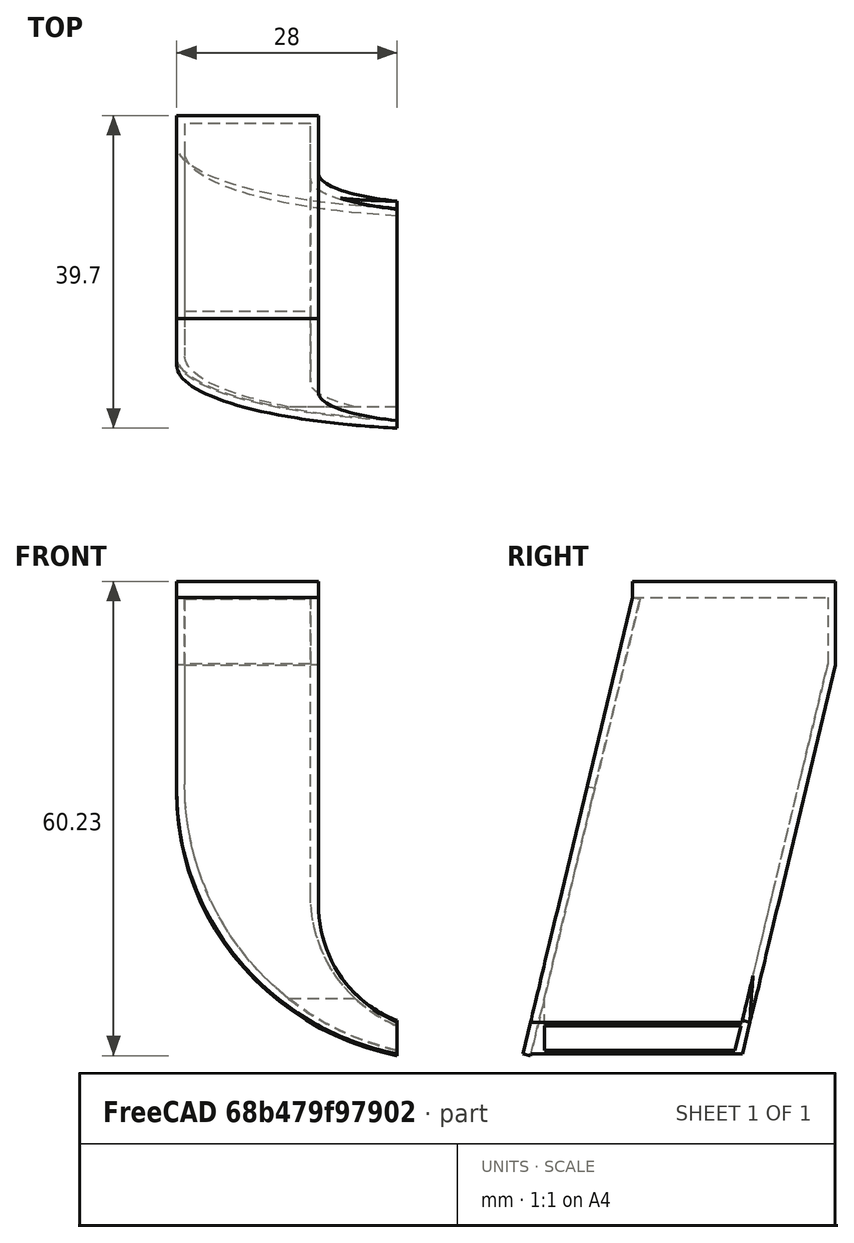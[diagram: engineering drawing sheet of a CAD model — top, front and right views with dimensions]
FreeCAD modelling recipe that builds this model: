
FCSTD DOCUMENT  (FreeCAD 0.19R)
Label: FanDuct9.2
License: All rights reserved
LicenseURL: http://en.wikipedia.org/wiki/All_rights_reserved
objects: Sketcher::SketchObject×15, PartDesign::Pad×5, PartDesign::Pocket×4, PartDesign::Body×1
note: 34 computed .brp shape members not serialized (recipe doc carries the construction recipe); baked Part::Feature solids carry a one-line shape summary decoded from their .brp

FEATURE [Sketcher::SketchObject] Sketch
  FullyConstrained = true
  MapMode = 5
  Support = -> [XY_Plane]
  sketch-geometry (5):
    g0: LineSegment StartX=0 StartY=0 StartZ=0 EndX=44 EndY=0 EndZ=0
    g1: LineSegment StartX=-14 StartY=0 StartZ=0 EndX=0 EndY=0 EndZ=0
    g2: LineSegment StartX=-14 StartY=0 StartZ=0 EndX=-14 EndY=-60.5 EndZ=0
    g3: LineSegment StartX=-14 StartY=-60.5 StartZ=0 EndX=44 EndY=-60.5 EndZ=0
    g4: LineSegment StartX=44 StartY=-60.5 StartZ=0 EndX=44 EndY=0 EndZ=0
  constraints (14):
    c: Coincident(g-1,g0)
    c: PointOnObject(g0,g-1)
    c: PointOnObject(g1,g-1)
    c: Coincident(g1,g0)
    c: Coincident(g1,g2)
    c: Vertical(g2)
    c: Coincident(g2,g3)
    c: Horizontal(g3)
    c: Coincident(g3,g4)
    c: Coincident(g4,g0)
    c: Vertical(g4)
    c: Distance(g4) = 60.5
    c: DistanceX(g0) = 44
    c: DistanceX(g1) = -14
FEATURE [Sketcher::SketchObject] Sketch035  label="startingpos"
  FullyConstrained = true
  MapMode = 5
  Placement = pos=(-14,0,0) rot=(0.57735,-0.57735,-0.57735;2.0944rad)
  sketch-geometry (9):
    g0: Circle CenterX=35 CenterY=-20 CenterZ=0 NormalX=0 NormalY=0 NormalZ=1 AngleXU=0 Radius=1
    g1: Circle CenterX=12 CenterY=44 CenterZ=0 NormalX=0 NormalY=0 NormalZ=1 AngleXU=0 Radius=1.9
    g2: Circle CenterX=55 CenterY=44 CenterZ=0 NormalX=0 NormalY=0 NormalZ=1 AngleXU=0 Radius=1.9
    g3: LineSegment StartX=12.5 StartY=38 StartZ=0 EndX=35 EndY=38 EndZ=0
    g4: LineSegment StartX=11 StartY=39 StartZ=0 EndX=59 EndY=39 EndZ=0
    g5: LineSegment StartX=59 StartY=39 StartZ=0 EndX=59 EndY=-19 EndZ=0
    g6: LineSegment StartX=59 StartY=-19 StartZ=0 EndX=11 EndY=-19 EndZ=0
    g7: LineSegment StartX=11 StartY=-19 StartZ=0 EndX=11 EndY=39 EndZ=0
    g8: GeomPoint X=35 Y=-19 Z=0
  constraints (26):
    c: DistanceY(g0) = -20
    c: Diameter(g1) = 3.8
    c: Equal(g1,g2)
    c: DistanceX(g1) = 12
    c: DistanceY(g1) = 44
    c: DistanceX(g2) = 55
    c: DistanceY(g2) = 44
    c: Diameter(g0) = 2
    c: Horizontal(g3)
    c: Distance(g3) = 22.5
    c: DistanceX(g0) = 35
    c: DistanceX(g3) = 35
    c: DistanceY(g3) = 38
    c: Coincident(g4,g5)
    c: Coincident(g5,g6)
    c: Coincident(g6,g7)
    c: Coincident(g7,g4)
    c: Horizontal(g4)
    c: Horizontal(g6)
    c: Vertical(g5)
    c: Vertical(g7)
    c: Distance(g6) = 48
    c: Symmetric(g6,g5,g8)
    c: DistanceX(g8) = 35
    c: DistanceY(g4) = 39
    c: DistanceY(g6) = -19
FEATURE [PartDesign::Pad] Pad
  Direction = (1,1,1)
  Length = 18
  Length2 = 10
  Placement = pos=(-14,0,0) rot=(0.57735,-0.57735,-0.57735;2.0944rad)
  Profile = -> Sketch035
  Type = 4
FEATURE [Sketcher::SketchObject] Sketch037  label="startingpos001"
  ExternalGeometry = -> [Pad]
  FullyConstrained = false
  MapMode = 5
  Placement = pos=(-32,0,2e-15) rot=(0.57735,-0.57735,-0.57735;2.0944rad)
  Support = -> [Pad]
  sketch-geometry (11):
    g0: Circle CenterX=35 CenterY=-20 CenterZ=0 NormalX=0 NormalY=0 NormalZ=1 AngleXU=0 Radius=1
    g1: Circle CenterX=12 CenterY=44 CenterZ=0 NormalX=0 NormalY=0 NormalZ=1 AngleXU=0 Radius=1.9
    g2: Circle CenterX=55 CenterY=44 CenterZ=0 NormalX=0 NormalY=0 NormalZ=1 AngleXU=0 Radius=1.9
    g3: LineSegment StartX=12.5 StartY=38 StartZ=0 EndX=35 EndY=38 EndZ=0
    g4: LineSegment StartX=5.2832 StartY=54.2913 StartZ=0 EndX=25.5067 EndY=-30.1947 EndZ=0
    g5: LineSegment StartX=25.5067 StartY=-30.1947 StartZ=0 EndX=-54.6701 EndY=-30.1947 EndZ=0
    g6: LineSegment StartX=-54.6701 StartY=-30.1947 StartZ=0 EndX=-35.1899 EndY=60.5708 EndZ=0
    g7: LineSegment StartX=-35.1899 StartY=60.5708 StartZ=0 EndX=99.6909 EndY=60.5708 EndZ=0
    g8: LineSegment StartX=63.1501 StartY=-71.009 StartZ=0 EndX=31.7121 EndY=60.3269 EndZ=0
    g9: LineSegment StartX=31.7121 StartY=60.3269 StartZ=0 EndX=5.2832 EndY=54.2913 EndZ=0
    g10: LineSegment StartX=63.1501 StartY=-71.009 StartZ=0 EndX=99.6909 EndY=60.5708 EndZ=0
  constraints (32):
    c: DistanceY(g0) = -20
    c: Diameter(g1) = 3.8
    c: Equal(g1,g2)
    c: DistanceX(g1) = 12
    c: DistanceY(g1) = 44
    c: DistanceX(g2) = 55
    c: DistanceY(g2) = 44
    c: Diameter(g0) = 2
    c: Horizontal(g3)
    c: Distance(g3) = 22.5
    c: DistanceX(g0) = 35
    c: DistanceX(g3) = 35
    c: DistanceY(g3) = 38
    c: Horizontal(g5)
    c: Coincident(g5,g6)
    c: Coincident(g6,g7)
    c: Horizontal(g7)
    c: Coincident(g8,g9)
    c: Coincident(g9,g4)
    c: Distance(g3,g8) = 2
    c: Coincident(g5,g4)
    c: Coincident(g8,g10)
    c: Coincident(g10,g7)
    c: DistanceX(g8) = 63.1501
    c: DistanceX(g4) = 25.5067
    c: DistanceX(g7) = 99.6909
    c: DistanceY(g7) = 60.5708
    c: DistanceX(g6) = -35.1899
    c: DistanceX(g5) = -54.6701
    c: DistanceX(g8) = 31.7121
    c: Distance(g-4,g4) = 2
    c: Parallel(g8,g4)
FEATURE [PartDesign::Pocket] Pocket
  BaseFeature = -> Pad
  Length = 5
  Length2 = 100
  Placement = pos=(-14,0,0) rot=(0.57735,-0.57735,-0.57735;2.0944rad)
  Profile = -> Sketch037
  Type = 1
FEATURE [Sketcher::SketchObject] Sketch038
  FullyConstrained = true
  MapMode = 5
  Placement = pos=(-14,-11,1.2e-15) rot=(0.57735,-0.57735,-0.57735;4.18879rad)
  Support = -> [Pocket]
  sketch-geometry (4):
    g0: LineSegment StartX=-54.22 StartY=0 StartZ=0 EndX=7.1e-15 EndY=0 EndZ=0
    g1: LineSegment StartX=-54.22 StartY=0 StartZ=0 EndX=-54.22 EndY=-31.06 EndZ=0
    g2: LineSegment StartX=-54.22 StartY=-31.06 StartZ=0 EndX=6.64 EndY=-31.06 EndZ=0
    g3: ArcOfCircle CenterX=2e-15 CenterY=-16.2397 CenterZ=0 NormalX=0 NormalY=0 NormalZ=1 AngleXU=0 Radius=16.2397 StartAngle=5.13361 EndAngle=7.85398
  constraints (11):
    c: Coincident(g0,g1)
    c: Vertical(g1)
    c: Coincident(g1,g2)
    c: Horizontal(g2)
    c: Coincident(g0,g-1)
    c: Tangent(g3,g0) = 1.5708
    c: PointOnObject(g0,g-1)
    c: Coincident(g2,g3)
    c: DistanceX(g1) = -54.22
    c: Distance(g1) = 31.06
    c: DistanceX(g2) = 6.64
FEATURE [PartDesign::Pocket] Pocket001
  BaseFeature = -> Pocket
  Length = 5
  Length2 = 100
  Placement = pos=(-14,0,0) rot=(0.57735,-0.57735,-0.57735;2.0944rad)
  Profile = -> Sketch038
  Type = 1
FEATURE [Sketcher::SketchObject] Sketch039
  ExternalGeometry = -> [Pocket001]
  FullyConstrained = true
  MapMode = 5
  Placement = pos=(-14,-11,1.2e-15) rot=(0.57735,-0.57735,-0.57735;4.18879rad)
  Support = -> [Pocket001]
  sketch-geometry (6):
    g0: LineSegment StartX=-54.0932 StartY=18 StartZ=0 EndX=-15 EndY=18 EndZ=0
    g1: ArcOfCircle CenterX=-15 CenterY=-16.6429 CenterZ=0 NormalX=0 NormalY=0 NormalZ=1 AngleXU=0 Radius=34.6429 StartAngle=0.192948 EndAngle=1.5708
    g2: LineSegment StartX=19 StartY=-10 StartZ=0 EndX=21.0808 EndY=-20.6504 EndZ=0
    g3: LineSegment StartX=21.0808 StartY=-20.6504 StartZ=0 EndX=53.1738 EndY=36.3726 EndZ=0
    g4: LineSegment StartX=53.1738 StartY=36.3726 StartZ=0 EndX=-65.4035 EndY=96.8279 EndZ=0
    g5: LineSegment StartX=-65.4035 StartY=96.8279 StartZ=0 EndX=-54.0932 EndY=18 EndZ=0
  constraints (16):
    c: Horizontal(g0)
    c: DistanceY(g0) = 18
    c: Tangent(g1,g0) = 1.5708
    c: Coincident(g1,g-3)
    c: Tangent(g1,g2) = 1.5708
    c: Coincident(g2,g3)
    c: Coincident(g3,g4)
    c: Coincident(g4,g5)
    c: Coincident(g5,g0)
    c: DistanceX(g0) = -15
    c: DistanceX(g0) = -54.0932
    c: DistanceX(g3) = 53.1738
    c: DistanceY(g3) = 36.3726
    c: DistanceX(g2) = 21.0808
    c: DistanceX(g4) = -65.4035
    c: DistanceY(g4) = 96.8279
FEATURE [PartDesign::Pocket] Pocket002
  BaseFeature = -> Pocket001
  Length = 5
  Length2 = 100
  Placement = pos=(-14,0,0) rot=(0.57735,-0.57735,-0.57735;2.0944rad)
  Profile = -> Sketch039
  Type = 1
FEATURE [Sketcher::SketchObject] Sketch040
  FullyConstrained = true
  MapMode = 5
  Placement = pos=(-14,1.3e-14,39) rot=(0,0,1;1.5708rad)
  Support = -> [Pocket002]
  sketch-geometry (4):
    g0: LineSegment StartX=-34.5 StartY=16.22 StartZ=0 EndX=-12 EndY=16.22 EndZ=0
    g1: LineSegment StartX=-12 StartY=16.22 StartZ=0 EndX=-12 EndY=0 EndZ=0
    g2: LineSegment StartX=-12 StartY=0 StartZ=0 EndX=-34.5 EndY=0 EndZ=0
    g3: LineSegment StartX=-34.5 StartY=0 StartZ=0 EndX=-34.5 EndY=16.22 EndZ=0
  constraints (12):
    c: Coincident(g0,g1)
    c: Coincident(g1,g2)
    c: Coincident(g2,g3)
    c: Coincident(g3,g0)
    c: Horizontal(g0)
    c: Horizontal(g2)
    c: Vertical(g1)
    c: Vertical(g3)
    c: PointOnObject(g1,g-1)
    c: Distance(g1) = 16.22
    c: Distance(g0) = 22.5
    c: DistanceX(g1) = -12
FEATURE [Sketcher::SketchObject] Sketch041
  FullyConstrained = true
  MapMode = 5
  Placement = pos=(-14,-43.6514,10.4489) rot=(0.526544,-0.526544,0.667459;1.96449rad)
  Support = -> [Pocket002]
FEATURE [Sketcher::SketchObject] Sketch042
  FullyConstrained = true
  MapMode = 5
  Placement = pos=(-14,-17.2884,4.13834) rot=(0.617528,-0.617528,-0.487154;4.04823rad)
  Support = -> [Pocket002]
FEATURE [Sketcher::SketchObject] Sketch043
  FullyConstrained = false
  MapMode = 5
  Placement = pos=(-14,-11,1.2e-15) rot=(0.57735,-0.57735,-0.57735;4.18879rad)
  Support = -> [Pocket002]
  sketch-geometry (6):
    g0: LineSegment StartX=-15.2456 StartY=17 StartZ=0 EndX=-45.7577 EndY=17 EndZ=0
    g1: LineSegment StartX=-45.7577 StartY=17 StartZ=0 EndX=-45.7577 EndY=1 EndZ=0
    g2: LineSegment StartX=-45.7577 StartY=1 StartZ=0 EndX=-1.19913 EndY=1 EndZ=0
    g3: ArcOfCircle CenterX=-15.2456 CenterY=-17.6789 CenterZ=0 NormalX=0 NormalY=0 NormalZ=1 AngleXU=0 Radius=34.6789 StartAngle=6.15693 EndAngle=7.85398
    g4: ArcOfCircle CenterX=-1.19913 CenterY=-17.1326 CenterZ=0 NormalX=0 NormalY=0 NormalZ=1 AngleXU=0 Radius=18.1326 StartAngle=0.336596 EndAngle=1.5708
    g5: LineSegment StartX=15.916 StartY=-11.1439 StartZ=0 EndX=19.1573 EndY=-22.0455 EndZ=0
  constraints (11):
    c: Horizontal(g0)
    c: Coincident(g0,g1)
    c: Vertical(g1)
    c: Coincident(g1,g2)
    c: Horizontal(g2)
    c: DistanceY(g2) = 1
    c: DistanceY(g0) = 17
    c: Tangent(g3,g0) = -1.5708
    c: Tangent(g4,g2) = 1.5708
    c: Coincident(g5,g4)
    c: Coincident(g5,g3)
FEATURE [Sketcher::SketchObject] Sketch044
  FullyConstrained = true
  MapMode = 5
  Placement = pos=(-14,-11,1.2e-15) rot=(0.57735,-0.57735,-0.57735;4.18879rad)
  Support = -> [Pocket002]
FEATURE [PartDesign::Pocket] Pocket003
  BaseFeature = -> Pocket002
  Length = 37
  Length2 = 100
  Placement = pos=(-14,0,0) rot=(0.57735,-0.57735,-0.57735;2.0944rad)
  Profile = -> Sketch043
  Type = 0
FEATURE [Sketcher::SketchObject] Sketch045
  ExternalGeometry = -> [Pocket003]
  FullyConstrained = false
  MapMode = 5
  Placement = pos=(-14,-43.6514,10.4489) rot=(0.526544,-0.526544,0.667459;1.96449rad)
  Support = -> [Pocket003]
  sketch-geometry (6):
    g0: LineSegment StartX=4.67966 StartY=18 StartZ=0 EndX=29.3577 EndY=18 EndZ=0
    g1: LineSegment StartX=29.3577 StartY=18 StartZ=0 EndX=29.3577 EndY=-2.13e-14 EndZ=0
    g2: LineSegment StartX=29.3577 StartY=-2.13e-14 StartZ=0 EndX=-10.7441 EndY=-2.27907e-11 EndZ=0
    g3: ArcOfCircle CenterX=4.14584 CenterY=-17.1591 CenterZ=0 NormalX=0 NormalY=0 NormalZ=1 AngleXU=0 Radius=35.1632 StartAngle=1.55561 EndAngle=2.93656
    g4: ArcOfCircle CenterX=-11.0342 CenterY=-16.4365 CenterZ=0 NormalX=0 NormalY=0 NormalZ=1 AngleXU=0 Radius=16.439 StartAngle=1.55315 EndAngle=2.73929
    g5: LineSegment StartX=-30.2808 StartY=-10 StartZ=0 EndX=-26.1608 EndY=-10 EndZ=0
  constraints (12):
    c: Coincident(g-3,g0)
    c: Coincident(g0,g-3)
    c: Coincident(g0,g1)
    c: Coincident(g1,g-4)
    c: Coincident(g1,g2)
    c: Coincident(g2,g-4)
    c: Coincident(g3,g0)
    c: Coincident(g4,g2)
    c: Coincident(g5,g3)
    c: Coincident(g5,g4)
    c: Coincident(g3,g-7)
    c: Coincident(g4,g-7)
FEATURE [PartDesign::Pad] Pad001
  BaseFeature = -> Pocket003
  Direction = (1,1,1)
  Length = 1
  Length2 = 100
  Placement = pos=(-14,0,0) rot=(0.57735,-0.57735,-0.57735;2.0944rad)
  Profile = -> Sketch045
  Reversed = true
  Type = 0
FEATURE [Sketcher::SketchObject] Sketch046
  ExternalGeometry = -> [Pad001]
  FullyConstrained = false
  MapMode = 5
  Placement = pos=(-14,-17.2884,4.13834) rot=(0.617528,-0.617528,-0.487154;4.04823rad)
  Support = -> [Pad001]
  sketch-geometry (6):
    g0: LineSegment StartX=-11.1685 StartY=18 StartZ=0 EndX=-27.0125 EndY=18 EndZ=0
    g1: LineSegment StartX=-27.0125 StartY=18 StartZ=0 EndX=-27.0125 EndY=-2.13e-14 EndZ=0
    g2: LineSegment StartX=-27.0125 StartY=-2.13e-14 StartZ=0 EndX=4.25525 EndY=-3.6e-15 EndZ=0
    g3: ArcOfCircle CenterX=-11.5343 CenterY=-18.2824 CenterZ=0 NormalX=0 NormalY=0 NormalZ=1 AngleXU=0 Radius=36.2843 StartAngle=0.230295 EndAngle=1.56071
    g4: ArcOfCircle CenterX=4.79347 CenterY=-16.054 CenterZ=0 NormalX=0 NormalY=0 NormalZ=1 AngleXU=0 Radius=16.063 StartAngle=0.386438 EndAngle=1.60431
    g5: LineSegment StartX=19.672 StartY=-10 StartZ=0 EndX=23.792 EndY=-10 EndZ=0
  constraints (11):
    c: Coincident(g0,g1)
    c: Coincident(g1,g-5)
    c: Coincident(g1,g2)
    c: Coincident(g2,g-5)
    c: Coincident(g3,g0)
    c: Coincident(g3,g-8)
    c: Coincident(g0,g-4)
    c: Coincident(g4,g2)
    c: Coincident(g4,g-7)
    c: Coincident(g5,g4)
    c: Coincident(g5,g3)
FEATURE [PartDesign::Pad] Pad002
  BaseFeature = -> Pad001
  Direction = (1,1,1)
  Length = 1
  Length2 = 100
  Placement = pos=(-14,0,0) rot=(0.57735,-0.57735,-0.57735;2.0944rad)
  Profile = -> Sketch046
  Reversed = true
  Type = 0
FEATURE [Sketcher::SketchObject] Sketch047
  ExternalGeometry = -> [Pad002]
  FullyConstrained = true
  MapMode = 5
  Placement = pos=(-14,-11,1.2e-15) rot=(0.57735,-0.57735,-0.57735;4.18879rad)
  Support = -> [Pad002]
  sketch-geometry (4):
    g0: LineSegment StartX=-30.4087 StartY=18 StartZ=0 EndX=-30.4087 EndY=-1.07e-14 EndZ=0
    g1: LineSegment StartX=-30.4087 StartY=-1.07e-14 StartZ=0 EndX=-39 EndY=-1.42e-14 EndZ=0
    g2: LineSegment StartX=-39 StartY=-1.42e-14 StartZ=0 EndX=-39 EndY=18 EndZ=0
    g3: LineSegment StartX=-39 StartY=18 StartZ=0 EndX=-30.4087 EndY=18 EndZ=0
  constraints (8):
    c: Coincident(g-3,g0)
    c: Coincident(g0,g-4)
    c: Coincident(g0,g1)
    c: Coincident(g1,g-4)
    c: Coincident(g1,g2)
    c: Coincident(g2,g-3)
    c: Coincident(g2,g3)
    c: Coincident(g3,g0)
FEATURE [PartDesign::Pad] Pad003
  BaseFeature = -> Pad002
  Direction = (1,1,1)
  Length = 1
  Length2 = 100
  Placement = pos=(-14,0,0) rot=(0.57735,-0.57735,-0.57735;2.0944rad)
  Profile = -> Sketch047
  Reversed = true
  Type = 0
FEATURE [Sketcher::SketchObject] Sketch048
  ExternalGeometry = -> [Pad003,Sketch040]
  FullyConstrained = true
  MapMode = 5
  Placement = pos=(-14,3.03e-14,39) rot=(0,0,1;1.5708rad)
  Support = -> [Pad003]
  sketch-geometry (4):
    g0: LineSegment StartX=-36.8171 StartY=18 StartZ=0 EndX=-11 EndY=18 EndZ=0
    g1: LineSegment StartX=-11 StartY=18 StartZ=0 EndX=-11 EndY=-2.84e-14 EndZ=0
    g2: LineSegment StartX=-11 StartY=-2.84e-14 StartZ=0 EndX=-36.8171 EndY=-2.84e-14 EndZ=0
    g3: LineSegment StartX=-36.8171 StartY=-2.84e-14 StartZ=0 EndX=-36.8171 EndY=18 EndZ=0
  constraints (10):
    c: Coincident(g0,g1)
    c: Coincident(g1,g2)
    c: Coincident(g2,g3)
    c: Coincident(g3,g0)
    c: Horizontal(g0)
    c: Horizontal(g2)
    c: Vertical(g1)
    c: Vertical(g3)
    c: Coincident(g0,g-3)
    c: Coincident(g1,g-8)
FEATURE [PartDesign::Pad] Pad004
  BaseFeature = -> Pad003
  Direction = (1,1,1)
  Length = 2
  Length2 = 100
  Placement = pos=(-14,0,0) rot=(0.57735,-0.57735,-0.57735;2.0944rad)
  Profile = -> Sketch048
  Type = 0
FEATURE [Sketcher::SketchObject] Sketch049
  FullyConstrained = true
  MapMode = 5
  Placement = pos=(-14,3.84e-14,41) rot=(0,0,1;1.5708rad)
  Support = -> [Pad004]
  sketch-geometry (4):
    g0: LineSegment StartX=-34.5 StartY=16.2 StartZ=0 EndX=-12 EndY=16.2 EndZ=0
    g1: LineSegment StartX=-12 StartY=16.2 StartZ=0 EndX=-12 EndY=0 EndZ=0
    g2: LineSegment StartX=-12 StartY=0 StartZ=0 EndX=-34.5 EndY=0 EndZ=0
    g3: LineSegment StartX=-34.5 StartY=0 StartZ=0 EndX=-34.5 EndY=16.2 EndZ=0
  constraints (12):
    c: Coincident(g0,g1)
    c: Coincident(g1,g2)
    c: Coincident(g2,g3)
    c: Coincident(g3,g0)
    c: Horizontal(g0)
    c: Horizontal(g2)
    c: Vertical(g1)
    c: Vertical(g3)
    c: PointOnObject(g1,g-1)
    c: DistanceX(g1) = -12
    c: Distance(g0) = 22.5
    c: Distance(g1) = 16.2
FEATURE [PartDesign::Body] Body
  Group = -> [Sketch,Sketch035,Pad,Sketch037,Pocket,Sketch038,Pocket001,Sketch039,Pocket002,Sketch040,Sketch041,Sketch042,Sketch043,Sketch044,Pocket003,Sketch045,Pad001,Sketch046,Pad002,Sketch047,Pad003,Sketch048,Pad004,Sketch049]
  Origin = -> Origin
  Tip = -> Pad004
